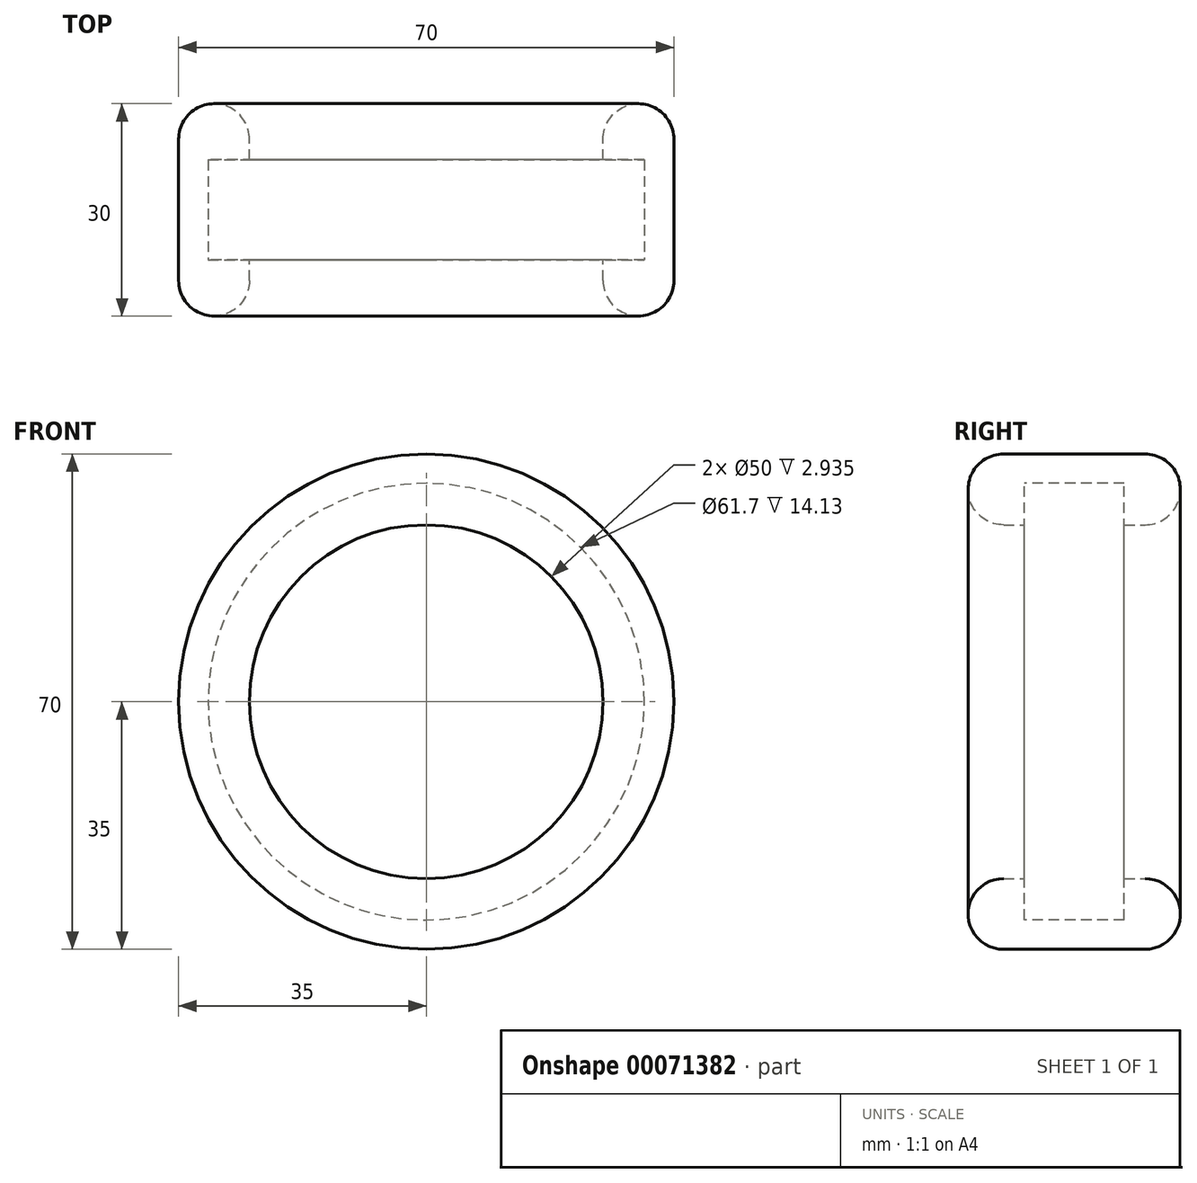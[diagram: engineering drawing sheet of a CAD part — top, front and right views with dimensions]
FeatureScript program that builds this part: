
annotation { "Feature Type Name" : "Feature", "Feature Type Description" : "" }
export const myFeature = defineFeature(function(context is Context, id is Id, definition is map)
    precondition{}
    {
        {
            var Q0;
            Q0=qCreatedBy(makeId("Front.planeOp"),FACE);
            var sketch = newSketch(context, id + "F0", { "sketchPlane" : qUnion([Q0])});
            skCircle(sketch, "E0", {"center": v(0, 0) * mm, "radius": 25 * mm});
            skCircle(sketch, "E1", {"center": v(0, 0) * mm, "radius": 35 * mm});
            skSolve(sketch);
        }
        {
            var Q0;
            Q0=makeQuery(id+"F0.imprint","IMPRINT",FACE,{"disambiguationData":[TD([[makeQuery(id+"F0.imprint","IMPRINT",EDGE,{"derivedFrom":sQuery(id+"F0.wireOp",EDGE,"E0")}),-1.0]])]});
            extrude(context, id + "F1", {"entities" : qUnion([Q0]), "depth" : 30 * mm, "symmetric" : true});
        }
        {
            var Q0;
            Q0=makeQuery(id+"F1.opExtrude","CAP_FACE",FACE,{"disambiguationData":[OSD([sQuery(id+"F0.wireOp",EDGE,"E0"),sQuery(id+"F0.wireOp",EDGE,"E1")])],"isStart":false});
            var Q1;
            Q1=makeQuery(id+"F1.opExtrude","CAP_FACE",FACE,{"disambiguationData":[OSD([sQuery(id+"F0.wireOp",EDGE,"E0"),sQuery(id+"F0.wireOp",EDGE,"E1")])],"isStart":true});
            fillet(context, id + "F2", {"entities" : qUnion([Q0, Q1]), "radius" : 5 * mm, "tangentPropagation" : true, "allowEdgeOverflow" : false});
        }
        {
            var Q0;
            Q0=qCreatedBy(makeId("Front.planeOp"),FACE);
            var sketch = newSketch(context, id + "F3", { "sketchPlane" : qUnion([Q0])});
            skCircle(sketch, "E2", {"center": v(0, 0) * mm, "radius": 30.85 * mm});
            skCircle(sketch, "E3", {"center": v(0, 0) * mm, "radius": 25.79 * mm});
            skSolve(sketch);
        }
        {
            var Q0;
            Q0 = qSketchRegion(id + "F3", true);
            var Q1;
            Q1=makeQuery(id+"F3.imprint","IMPRINT",FACE,{"disambiguationData":[TD([[makeQuery(id+"F3.imprint","IMPRINT",EDGE,{"derivedFrom":sQuery(id+"F3.wireOp",EDGE,"E3")}),1.0]])]});
            extrude(context, id + "F4", {"entities" : qUnion([Q0, Q1]), "operationType" : NewBodyOperationType.REMOVE, "oppositeDirection" : true, "depth" : 14.13 * mm, "symmetric" : true});
        }
    });
